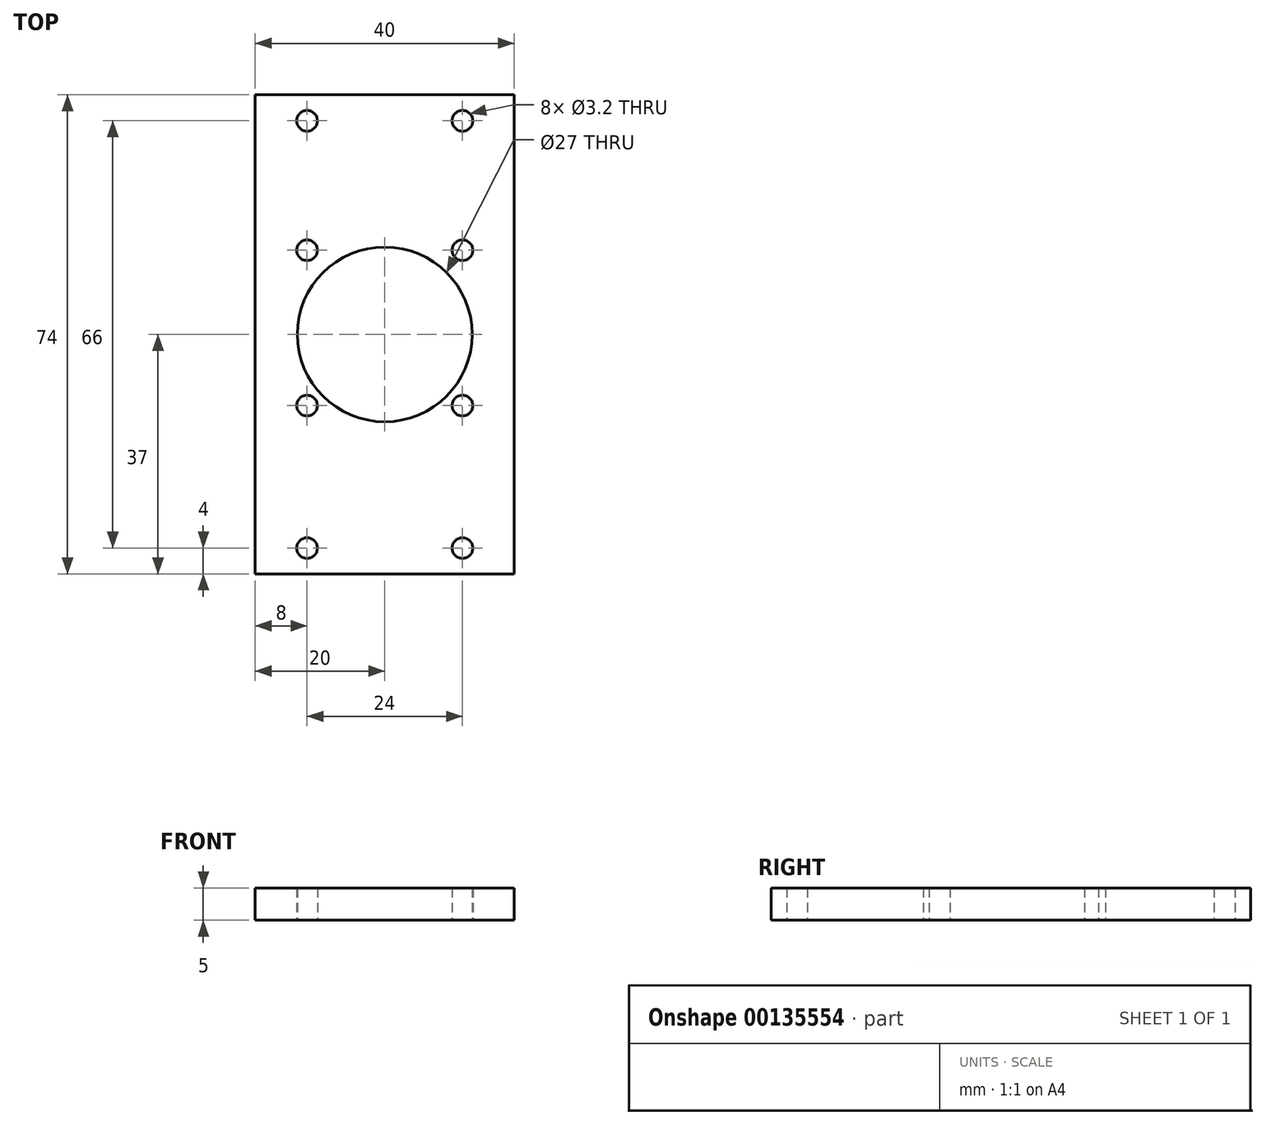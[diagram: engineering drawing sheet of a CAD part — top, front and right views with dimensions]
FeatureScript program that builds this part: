
annotation { "Feature Type Name" : "Feature", "Feature Type Description" : "" }
export const myFeature = defineFeature(function(context is Context, id is Id, definition is map)
    precondition{}
    {
        {
            var Q0;
            Q0=qCreatedBy(makeId("Top.planeOp"),FACE);
            var sketch = newSketch(context, id + "F0", { "sketchPlane" : qUnion([Q0])});
            skLineSegment(sketch, "E0.bottom", {"start": v(-15, 16) * mm, "end": v(15, 16) * mm, "construction": true});
            skLineSegment(sketch, "E0.top", {"start": v(-15, -14) * mm, "end": v(15, -14) * mm, "construction": true});
            skLineSegment(sketch, "E0.left", {"start": v(-15, 16) * mm, "end": v(-15, -14) * mm, "construction": true});
            skLineSegment(sketch, "E0.right", {"start": v(15, 16) * mm, "end": v(15, -14) * mm, "construction": true});
            skLineSegment(sketch, "E1.bottom", {"start": v(-12, 13) * mm, "end": v(12, 13) * mm, "construction": true});
            skLineSegment(sketch, "E1.top", {"start": v(-12, -11) * mm, "end": v(12, -11) * mm, "construction": true});
            skLineSegment(sketch, "E1.left", {"start": v(-12, 13) * mm, "end": v(-12, -11) * mm, "construction": true});
            skLineSegment(sketch, "E1.right", {"start": v(12, 13) * mm, "end": v(12, -11) * mm, "construction": true});
            skLineSegment(sketch, "E2.bottom", {"start": v(-20, 37) * mm, "end": v(20, 37) * mm, "construction": true});
            skLineSegment(sketch, "E2.top", {"start": v(-20, -37) * mm, "end": v(20, -37) * mm, "construction": true});
            skLineSegment(sketch, "E2.left", {"start": v(-20, 37) * mm, "end": v(-20, -37) * mm, "construction": true});
            skLineSegment(sketch, "E2.right", {"start": v(20, 37) * mm, "end": v(20, -37) * mm, "construction": true});
            skLineSegment(sketch, "E3", {"start": v(-20, 33) * mm, "end": v(20, 33) * mm, "construction": true});
            skLineSegment(sketch, "E4", {"start": v(-20, -33) * mm, "end": v(20, -33) * mm, "construction": true});
            skLineSegment(sketch, "E5", {"start": v(-15, 16) * mm, "end": v(-15, 37) * mm, "construction": true});
            skLineSegment(sketch, "E6", {"start": v(12, 13) * mm, "end": v(12, 33) * mm, "construction": true});
            skLineSegment(sketch, "E7", {"start": v(12, -11) * mm, "end": v(12, -33) * mm, "construction": true});
            skLineSegment(sketch, "E8", {"start": v(-12, -11) * mm, "end": v(-12, -33) * mm, "construction": true});
            skLineSegment(sketch, "E9", {"start": v(-12, 13) * mm, "end": v(-12, 33) * mm, "construction": true});
            skCircle(sketch, "E10", {"center": v(-12, 13) * mm, "radius": 1.6 * mm});
            skCircle(sketch, "E11", {"center": v(12, 13) * mm, "radius": 1.6 * mm});
            skCircle(sketch, "E12", {"center": v(12, 33) * mm, "radius": 1.6 * mm});
            skCircle(sketch, "E13", {"center": v(-12, 33) * mm, "radius": 1.6 * mm});
            skCircle(sketch, "E14", {"center": v(-12, -11) * mm, "radius": 1.6 * mm});
            skCircle(sketch, "E15", {"center": v(12, -33) * mm, "radius": 1.6 * mm});
            skCircle(sketch, "E16", {"center": v(-12, -33) * mm, "radius": 1.6 * mm});
            skCircle(sketch, "E17", {"center": v(12, -11) * mm, "radius": 1.6 * mm});
            skLineSegment(sketch, "E18", {"start": v(-20, 37) * mm, "end": v(-20, -37) * mm});
            skLineSegment(sketch, "E19", {"start": v(-20, -37) * mm, "end": v(20, -37) * mm});
            skLineSegment(sketch, "E20", {"start": v(20, -37) * mm, "end": v(20, 37) * mm});
            skLineSegment(sketch, "E21", {"start": v(20, 37) * mm, "end": v(-20, 37) * mm});
            skCircle(sketch, "E22", {"center": v(0, 0) * mm, "radius": 13.5 * mm});
            skSolve(sketch);
        }
        {
            var Q0;
            Q0 = qSketchRegion(id + "F0", true);
            extrude(context, id + "F1", {"entities" : qUnion([Q0]), "depth" : 5 * mm});
        }
    });
